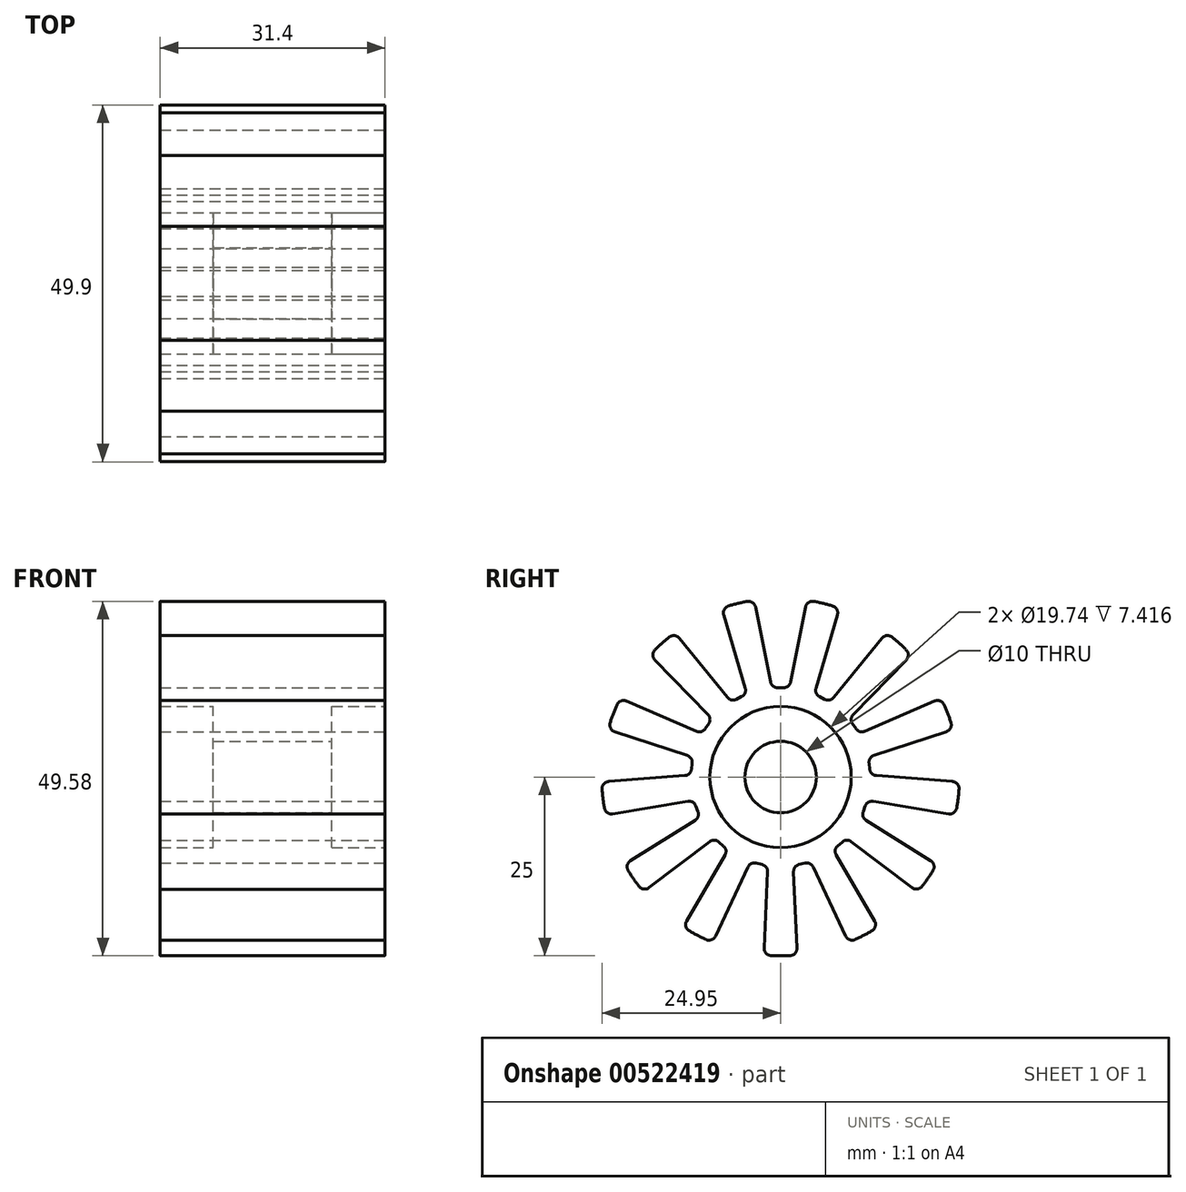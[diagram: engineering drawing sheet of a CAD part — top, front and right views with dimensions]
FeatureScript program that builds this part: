
annotation { "Feature Type Name" : "Feature", "Feature Type Description" : "" }
export const myFeature = defineFeature(function(context is Context, id is Id, definition is map)
    precondition{}
    {
        {
            var Q0;
            Q0=qCreatedBy(makeId("Top.planeOp"),FACE);
            var sketch = newSketch(context, id + "F0", { "sketchPlane" : qUnion([Q0])});
            skLineSegment(sketch, "E0", {"start": v(-8.28, 5) * mm, "end": v(-8.28, 9.87) * mm});
            skLineSegment(sketch, "E1", {"start": v(-8.28, 9.87) * mm, "end": v(-15.7, 9.87) * mm});
            skLineSegment(sketch, "E2", {"start": v(-15.7, 9.87) * mm, "end": v(-15.7, 25) * mm});
            skLineSegment(sketch, "E3", {"start": v(-15.7, 25) * mm, "end": v(15.7, 25) * mm});
            skLineSegment(sketch, "E4", {"start": v(15.7, 25) * mm, "end": v(15.7, 9.87) * mm});
            skLineSegment(sketch, "E5", {"start": v(15.7, 9.87) * mm, "end": v(8.28, 9.87) * mm});
            skLineSegment(sketch, "E6", {"start": v(8.28, 9.87) * mm, "end": v(8.28, 5) * mm});
            skLineSegment(sketch, "E7", {"start": v(-8.28, 5) * mm, "end": v(8.28, 5) * mm});
            skLineSegment(sketch, "E8.MirrorCS", {"start": v(-15.7, -9.87) * mm, "end": v(-15.7, -25) * mm});
            skLineSegment(sketch, "E9.MirrorCS", {"start": v(-8.28, -9.87) * mm, "end": v(-15.7, -9.87) * mm});
            skLineSegment(sketch, "E10.MirrorCS", {"start": v(-8.28, -5) * mm, "end": v(8.28, -5) * mm, "construction": true});
            skLineSegment(sketch, "E11.MirrorCS", {"start": v(8.28, -9.87) * mm, "end": v(8.28, -5) * mm});
            skLineSegment(sketch, "E12.MirrorCS", {"start": v(15.7, -9.87) * mm, "end": v(8.28, -9.87) * mm});
            skLineSegment(sketch, "E13.MirrorCS", {"start": v(15.7, -25) * mm, "end": v(15.7, -9.87) * mm});
            skLineSegment(sketch, "E14.MirrorCS", {"start": v(-15.7, -25) * mm, "end": v(15.7, -25) * mm});
            skLineSegment(sketch, "E15.MirrorCS", {"start": v(-8.28, -5) * mm, "end": v(-8.28, -9.87) * mm});
            skLineSegment(sketch, "E16", {"start": v(0, 0) * mm, "end": v(-18.91, 0) * mm});
            skSolve(sketch);
        }
        {
            var Q0;
            Q0=makeQuery(id+"F0.imprint","IMPRINT",FACE,{"disambiguationData":[TD([[makeQuery(id+"F0.imprint","IMPRINT",EDGE,{"derivedFrom":sQuery(id+"F0.wireOp",EDGE,"E0")}),-1.0]])]});
            var Q1;
            Q1=sQuery(id+"F0.wireOp",EDGE,"E16");
            revolve(context, id + "F1", {"entities" : qUnion([Q0]), "axis" : qUnion([Q1]), "revolveType" : RevolveType.FULL});
        }
        {
            var Q0;
            Q0=makeQuery(id+"F1.opRevolve","SWEPT_FACE",FACE,{"disambiguationData":[OSD([sQuery(id+"F0.wireOp",EDGE,"E4")])]});
            var sketch = newSketch(context, id + "F2", { "sketchPlane" : qUnion([Q0])});
            skLineSegment(sketch, "E17", {"start": v(-3.75, 25) * mm, "end": v(3.75, 25) * mm});
            skLineSegment(sketch, "E18", {"start": v(3.75, 25) * mm, "end": v(1.41, 13.3) * mm});
            skLineSegment(sketch, "E19", {"start": v(0.43, 12.5) * mm, "end": v(-0.43, 12.5) * mm});
            skLineSegment(sketch, "E20", {"start": v(-1.41, 13.3) * mm, "end": v(-3.75, 25) * mm});
            skLineSegment(sketch, "E21", {"start": v(0, 25) * mm, "end": v(0, 12.5) * mm});
            skPoint(sketch, "E22.visualSharp", {"position": v(-1.25, 12.5) * mm});
            skArc(sketch, "E22.filletArc", {"start": v(-1.41, 13.3) * mm, "mid": v(-1.06, 12.73) * mm, "end": v(-0.43, 12.5) * mm});
            skPoint(sketch, "E23.visualSharp", {"position": v(1.25, 12.5) * mm});
            skArc(sketch, "E23.filletArc", {"start": v(0.43, 12.5) * mm, "mid": v(1.06, 12.73) * mm, "end": v(1.41, 13.3) * mm});
            skSolve(sketch);
        }
        {
            var Q0;
            Q0 = qSketchRegion(id + "F2", true);
            extrude(context, id + "F3", {"entities" : qUnion([Q0]), "operationType" : NewBodyOperationType.REMOVE, "oppositeDirection" : true, "depth" : 35 * mm, "offsetDistance" : 25 * mm});
        }
        {
            var Q0;
            Q0=makeQuery(id+"F3.boolean.opBoolean","COPY",FACE,{"derivedFrom":makeQuery(id+"F3.opExtrude","SWEPT_FACE",FACE,{"disambiguationData":[OSD([sQuery(id+"F2.wireOp",EDGE,"E18")])]})});
            var Q1;
            Q1=makeQuery(id+"F3.boolean.opBoolean","COPY",FACE,{"derivedFrom":makeQuery(id+"F3.opExtrude","SWEPT_FACE",FACE,{"disambiguationData":[OSD([sQuery(id+"F2.wireOp",EDGE,"E23.filletArc")])]})});
            var Q2;
            Q2=makeQuery(id+"F3.boolean.opBoolean","COPY",FACE,{"derivedFrom":makeQuery(id+"F3.opExtrude","SWEPT_FACE",FACE,{"disambiguationData":[OSD([sQuery(id+"F2.wireOp",EDGE,"E19")])]})});
            var Q3;
            Q3=makeQuery(id+"F3.boolean.opBoolean","COPY",FACE,{"derivedFrom":makeQuery(id+"F3.opExtrude","SWEPT_FACE",FACE,{"disambiguationData":[OSD([sQuery(id+"F2.wireOp",EDGE,"E22.filletArc")])]})});
            var Q4;
            Q4=makeQuery(id+"F3.boolean.opBoolean","COPY",FACE,{"derivedFrom":makeQuery(id+"F3.opExtrude","SWEPT_FACE",FACE,{"disambiguationData":[OSD([sQuery(id+"F2.wireOp",EDGE,"E20")])]})});
            var Q5;
            Q5=makeQuery(id+"F1.opRevolve","SWEPT_FACE",FACE,{"disambiguationData":[OSD([sQuery(id+"F0.wireOp",EDGE,"E3")])]});
            circularPattern(context, id + "F4", {"patternType" : PatternType.FACE, "operationType" : NewBodyOperationType.REMOVE, "faces" : qUnion([Q0, Q1, Q2, Q3, Q4]), "axis" : qUnion([Q5]), "angle" : 360 * degree, "instanceCount" : 13, "equalSpace" : true});
        }
        {
            var Q0;
            Q0=makeQuery(id+"F4.opPattern","COPY",EDGE,{"derivedFrom":makeQuery(id+"F3.boolean.opBoolean","INTERSECT",EDGE,{"derivedFrom":[makeQuery(id+"F1.opRevolve","SWEPT_FACE",FACE,{"disambiguationData":[OSD([sQuery(id+"F0.wireOp",EDGE,"E3")])]}),makeQuery(id+"F3.opExtrude","SWEPT_FACE",FACE,{"disambiguationData":[OSD([sQuery(id+"F2.wireOp",EDGE,"E18")])]})]}),"instanceName":"1"});
            var Q1;
            Q1=makeQuery(id+"F3.boolean.opBoolean","INTERSECT",EDGE,{"derivedFrom":[makeQuery(id+"F1.opRevolve","SWEPT_FACE",FACE,{"disambiguationData":[OSD([sQuery(id+"F0.wireOp",EDGE,"E3")])]}),makeQuery(id+"F3.opExtrude","SWEPT_FACE",FACE,{"disambiguationData":[OSD([sQuery(id+"F2.wireOp",EDGE,"E20")])]})]});
            var Q2;
            Q2=makeQuery(id+"F3.boolean.opBoolean","INTERSECT",EDGE,{"derivedFrom":[makeQuery(id+"F1.opRevolve","SWEPT_FACE",FACE,{"disambiguationData":[OSD([sQuery(id+"F0.wireOp",EDGE,"E3")])]}),makeQuery(id+"F3.opExtrude","SWEPT_FACE",FACE,{"disambiguationData":[OSD([sQuery(id+"F2.wireOp",EDGE,"E18")])]})]});
            var Q3;
            Q3=makeQuery(id+"F4.opPattern","COPY",EDGE,{"derivedFrom":makeQuery(id+"F3.boolean.opBoolean","INTERSECT",EDGE,{"derivedFrom":[makeQuery(id+"F1.opRevolve","SWEPT_FACE",FACE,{"disambiguationData":[OSD([sQuery(id+"F0.wireOp",EDGE,"E3")])]}),makeQuery(id+"F3.opExtrude","SWEPT_FACE",FACE,{"disambiguationData":[OSD([sQuery(id+"F2.wireOp",EDGE,"E20")])]})]}),"instanceName":"12"});
            var Q4;
            Q4=makeQuery(id+"F4.opPattern","COPY",EDGE,{"derivedFrom":makeQuery(id+"F3.boolean.opBoolean","INTERSECT",EDGE,{"derivedFrom":[makeQuery(id+"F1.opRevolve","SWEPT_FACE",FACE,{"disambiguationData":[OSD([sQuery(id+"F0.wireOp",EDGE,"E3")])]}),makeQuery(id+"F3.opExtrude","SWEPT_FACE",FACE,{"disambiguationData":[OSD([sQuery(id+"F2.wireOp",EDGE,"E18")])]})]}),"instanceName":"12"});
            var Q5;
            Q5=makeQuery(id+"F4.opPattern","COPY",EDGE,{"derivedFrom":makeQuery(id+"F3.boolean.opBoolean","INTERSECT",EDGE,{"derivedFrom":[makeQuery(id+"F1.opRevolve","SWEPT_FACE",FACE,{"disambiguationData":[OSD([sQuery(id+"F0.wireOp",EDGE,"E3")])]}),makeQuery(id+"F3.opExtrude","SWEPT_FACE",FACE,{"disambiguationData":[OSD([sQuery(id+"F2.wireOp",EDGE,"E20")])]})]}),"instanceName":"11"});
            var Q6;
            Q6=makeQuery(id+"F4.opPattern","COPY",EDGE,{"derivedFrom":makeQuery(id+"F3.boolean.opBoolean","INTERSECT",EDGE,{"derivedFrom":[makeQuery(id+"F1.opRevolve","SWEPT_FACE",FACE,{"disambiguationData":[OSD([sQuery(id+"F0.wireOp",EDGE,"E3")])]}),makeQuery(id+"F3.opExtrude","SWEPT_FACE",FACE,{"disambiguationData":[OSD([sQuery(id+"F2.wireOp",EDGE,"E18")])]})]}),"instanceName":"11"});
            var Q7;
            Q7=makeQuery(id+"F4.opPattern","COPY",EDGE,{"derivedFrom":makeQuery(id+"F3.boolean.opBoolean","INTERSECT",EDGE,{"derivedFrom":[makeQuery(id+"F1.opRevolve","SWEPT_FACE",FACE,{"disambiguationData":[OSD([sQuery(id+"F0.wireOp",EDGE,"E3")])]}),makeQuery(id+"F3.opExtrude","SWEPT_FACE",FACE,{"disambiguationData":[OSD([sQuery(id+"F2.wireOp",EDGE,"E20")])]})]}),"instanceName":"10"});
            var Q8;
            Q8=makeQuery(id+"F4.opPattern","COPY",EDGE,{"derivedFrom":makeQuery(id+"F3.boolean.opBoolean","INTERSECT",EDGE,{"derivedFrom":[makeQuery(id+"F1.opRevolve","SWEPT_FACE",FACE,{"disambiguationData":[OSD([sQuery(id+"F0.wireOp",EDGE,"E3")])]}),makeQuery(id+"F3.opExtrude","SWEPT_FACE",FACE,{"disambiguationData":[OSD([sQuery(id+"F2.wireOp",EDGE,"E18")])]})]}),"instanceName":"10"});
            var Q9;
            Q9=makeQuery(id+"F4.opPattern","COPY",EDGE,{"derivedFrom":makeQuery(id+"F3.boolean.opBoolean","INTERSECT",EDGE,{"derivedFrom":[makeQuery(id+"F1.opRevolve","SWEPT_FACE",FACE,{"disambiguationData":[OSD([sQuery(id+"F0.wireOp",EDGE,"E3")])]}),makeQuery(id+"F3.opExtrude","SWEPT_FACE",FACE,{"disambiguationData":[OSD([sQuery(id+"F2.wireOp",EDGE,"E20")])]})]}),"instanceName":"9"});
            var Q10;
            Q10=makeQuery(id+"F4.opPattern","COPY",EDGE,{"derivedFrom":makeQuery(id+"F3.boolean.opBoolean","INTERSECT",EDGE,{"derivedFrom":[makeQuery(id+"F1.opRevolve","SWEPT_FACE",FACE,{"disambiguationData":[OSD([sQuery(id+"F0.wireOp",EDGE,"E3")])]}),makeQuery(id+"F3.opExtrude","SWEPT_FACE",FACE,{"disambiguationData":[OSD([sQuery(id+"F2.wireOp",EDGE,"E18")])]})]}),"instanceName":"2"});
            var Q11;
            Q11=makeQuery(id+"F4.opPattern","COPY",EDGE,{"derivedFrom":makeQuery(id+"F3.boolean.opBoolean","INTERSECT",EDGE,{"derivedFrom":[makeQuery(id+"F1.opRevolve","SWEPT_FACE",FACE,{"disambiguationData":[OSD([sQuery(id+"F0.wireOp",EDGE,"E3")])]}),makeQuery(id+"F3.opExtrude","SWEPT_FACE",FACE,{"disambiguationData":[OSD([sQuery(id+"F2.wireOp",EDGE,"E20")])]})]}),"instanceName":"1"});
            var Q12;
            Q12=makeQuery(id+"F4.opPattern","COPY",EDGE,{"derivedFrom":makeQuery(id+"F3.boolean.opBoolean","INTERSECT",EDGE,{"derivedFrom":[makeQuery(id+"F1.opRevolve","SWEPT_FACE",FACE,{"disambiguationData":[OSD([sQuery(id+"F0.wireOp",EDGE,"E3")])]}),makeQuery(id+"F3.opExtrude","SWEPT_FACE",FACE,{"disambiguationData":[OSD([sQuery(id+"F2.wireOp",EDGE,"E18")])]})]}),"instanceName":"3"});
            var Q13;
            Q13=makeQuery(id+"F4.opPattern","COPY",EDGE,{"derivedFrom":makeQuery(id+"F3.boolean.opBoolean","INTERSECT",EDGE,{"derivedFrom":[makeQuery(id+"F1.opRevolve","SWEPT_FACE",FACE,{"disambiguationData":[OSD([sQuery(id+"F0.wireOp",EDGE,"E3")])]}),makeQuery(id+"F3.opExtrude","SWEPT_FACE",FACE,{"disambiguationData":[OSD([sQuery(id+"F2.wireOp",EDGE,"E20")])]})]}),"instanceName":"2"});
            var Q14;
            Q14=makeQuery(id+"F4.opPattern","COPY",EDGE,{"derivedFrom":makeQuery(id+"F3.boolean.opBoolean","INTERSECT",EDGE,{"derivedFrom":[makeQuery(id+"F1.opRevolve","SWEPT_FACE",FACE,{"disambiguationData":[OSD([sQuery(id+"F0.wireOp",EDGE,"E3")])]}),makeQuery(id+"F3.opExtrude","SWEPT_FACE",FACE,{"disambiguationData":[OSD([sQuery(id+"F2.wireOp",EDGE,"E18")])]})]}),"instanceName":"4"});
            var Q15;
            Q15=makeQuery(id+"F4.opPattern","COPY",EDGE,{"derivedFrom":makeQuery(id+"F3.boolean.opBoolean","INTERSECT",EDGE,{"derivedFrom":[makeQuery(id+"F1.opRevolve","SWEPT_FACE",FACE,{"disambiguationData":[OSD([sQuery(id+"F0.wireOp",EDGE,"E3")])]}),makeQuery(id+"F3.opExtrude","SWEPT_FACE",FACE,{"disambiguationData":[OSD([sQuery(id+"F2.wireOp",EDGE,"E20")])]})]}),"instanceName":"3"});
            var Q16;
            Q16=makeQuery(id+"F4.opPattern","COPY",EDGE,{"derivedFrom":makeQuery(id+"F3.boolean.opBoolean","INTERSECT",EDGE,{"derivedFrom":[makeQuery(id+"F1.opRevolve","SWEPT_FACE",FACE,{"disambiguationData":[OSD([sQuery(id+"F0.wireOp",EDGE,"E3")])]}),makeQuery(id+"F3.opExtrude","SWEPT_FACE",FACE,{"disambiguationData":[OSD([sQuery(id+"F2.wireOp",EDGE,"E20")])]})]}),"instanceName":"4"});
            var Q17;
            Q17=makeQuery(id+"F4.opPattern","COPY",EDGE,{"derivedFrom":makeQuery(id+"F3.boolean.opBoolean","INTERSECT",EDGE,{"derivedFrom":[makeQuery(id+"F1.opRevolve","SWEPT_FACE",FACE,{"disambiguationData":[OSD([sQuery(id+"F0.wireOp",EDGE,"E3")])]}),makeQuery(id+"F3.opExtrude","SWEPT_FACE",FACE,{"disambiguationData":[OSD([sQuery(id+"F2.wireOp",EDGE,"E18")])]})]}),"instanceName":"5"});
            var Q18;
            Q18=makeQuery(id+"F4.opPattern","COPY",EDGE,{"derivedFrom":makeQuery(id+"F3.boolean.opBoolean","INTERSECT",EDGE,{"derivedFrom":[makeQuery(id+"F1.opRevolve","SWEPT_FACE",FACE,{"disambiguationData":[OSD([sQuery(id+"F0.wireOp",EDGE,"E3")])]}),makeQuery(id+"F3.opExtrude","SWEPT_FACE",FACE,{"disambiguationData":[OSD([sQuery(id+"F2.wireOp",EDGE,"E20")])]})]}),"instanceName":"5"});
            var Q19;
            Q19=makeQuery(id+"F4.opPattern","COPY",EDGE,{"derivedFrom":makeQuery(id+"F3.boolean.opBoolean","INTERSECT",EDGE,{"derivedFrom":[makeQuery(id+"F1.opRevolve","SWEPT_FACE",FACE,{"disambiguationData":[OSD([sQuery(id+"F0.wireOp",EDGE,"E3")])]}),makeQuery(id+"F3.opExtrude","SWEPT_FACE",FACE,{"disambiguationData":[OSD([sQuery(id+"F2.wireOp",EDGE,"E18")])]})]}),"instanceName":"6"});
            var Q20;
            Q20=makeQuery(id+"F4.opPattern","COPY",EDGE,{"derivedFrom":makeQuery(id+"F3.boolean.opBoolean","INTERSECT",EDGE,{"derivedFrom":[makeQuery(id+"F1.opRevolve","SWEPT_FACE",FACE,{"disambiguationData":[OSD([sQuery(id+"F0.wireOp",EDGE,"E3")])]}),makeQuery(id+"F3.opExtrude","SWEPT_FACE",FACE,{"disambiguationData":[OSD([sQuery(id+"F2.wireOp",EDGE,"E20")])]})]}),"instanceName":"6"});
            var Q21;
            Q21=makeQuery(id+"F4.opPattern","COPY",EDGE,{"derivedFrom":makeQuery(id+"F3.boolean.opBoolean","INTERSECT",EDGE,{"derivedFrom":[makeQuery(id+"F1.opRevolve","SWEPT_FACE",FACE,{"disambiguationData":[OSD([sQuery(id+"F0.wireOp",EDGE,"E3")])]}),makeQuery(id+"F3.opExtrude","SWEPT_FACE",FACE,{"disambiguationData":[OSD([sQuery(id+"F2.wireOp",EDGE,"E18")])]})]}),"instanceName":"7"});
            var Q22;
            Q22=makeQuery(id+"F4.opPattern","COPY",EDGE,{"derivedFrom":makeQuery(id+"F3.boolean.opBoolean","INTERSECT",EDGE,{"derivedFrom":[makeQuery(id+"F1.opRevolve","SWEPT_FACE",FACE,{"disambiguationData":[OSD([sQuery(id+"F0.wireOp",EDGE,"E3")])]}),makeQuery(id+"F3.opExtrude","SWEPT_FACE",FACE,{"disambiguationData":[OSD([sQuery(id+"F2.wireOp",EDGE,"E20")])]})]}),"instanceName":"7"});
            var Q23;
            Q23=makeQuery(id+"F4.opPattern","COPY",EDGE,{"derivedFrom":makeQuery(id+"F3.boolean.opBoolean","INTERSECT",EDGE,{"derivedFrom":[makeQuery(id+"F1.opRevolve","SWEPT_FACE",FACE,{"disambiguationData":[OSD([sQuery(id+"F0.wireOp",EDGE,"E3")])]}),makeQuery(id+"F3.opExtrude","SWEPT_FACE",FACE,{"disambiguationData":[OSD([sQuery(id+"F2.wireOp",EDGE,"E18")])]})]}),"instanceName":"8"});
            var Q24;
            Q24=makeQuery(id+"F4.opPattern","COPY",EDGE,{"derivedFrom":makeQuery(id+"F3.boolean.opBoolean","INTERSECT",EDGE,{"derivedFrom":[makeQuery(id+"F1.opRevolve","SWEPT_FACE",FACE,{"disambiguationData":[OSD([sQuery(id+"F0.wireOp",EDGE,"E3")])]}),makeQuery(id+"F3.opExtrude","SWEPT_FACE",FACE,{"disambiguationData":[OSD([sQuery(id+"F2.wireOp",EDGE,"E20")])]})]}),"instanceName":"8"});
            var Q25;
            Q25=makeQuery(id+"F4.opPattern","COPY",EDGE,{"derivedFrom":makeQuery(id+"F3.boolean.opBoolean","INTERSECT",EDGE,{"derivedFrom":[makeQuery(id+"F1.opRevolve","SWEPT_FACE",FACE,{"disambiguationData":[OSD([sQuery(id+"F0.wireOp",EDGE,"E3")])]}),makeQuery(id+"F3.opExtrude","SWEPT_FACE",FACE,{"disambiguationData":[OSD([sQuery(id+"F2.wireOp",EDGE,"E18")])]})]}),"instanceName":"9"});
            fillet(context, id + "F5", {"entities" : qUnion([Q0, Q1, Q2, Q3, Q4, Q5, Q6, Q7, Q8, Q9, Q10, Q11, Q12, Q13, Q14, Q15, Q16, Q17, Q18, Q19, Q20, Q21, Q22, Q23, Q24, Q25]), "radius" : 1 * mm, "tangentPropagation" : true, "allowEdgeOverflow" : false});
        }
    });
